FCSTD DOCUMENT  (FreeCAD 0.17R12435 (Git))
Label: JST_ZE_top_entry_pad_size
License: All rights reserved
LicenseURL: http://en.wikipedia.org/wiki/All_rights_reserved
objects: Sketcher::SketchObject×1, PartDesign::Body×1, Spreadsheet::Sheet×1
note: 2 computed .brp shape members not serialized (recipe doc carries the construction recipe); baked Part::Feature solids carry a one-line shape summary decoded from their .brp

FEATURE [Sketcher::SketchObject] Sketch
  MapMode = 5
  Support = -> [XY_Plane]
  expr: Constraints[3] = 0.75 / 2
  sketch-geometry (26):
    g0: Circle CenterX=0 CenterY=0 CenterZ=0 NormalX=0 NormalY=0 NormalZ=1 AngleXU=0 Radius=0.375
    g1: Circle CenterX=1.5 CenterY=2 CenterZ=0 NormalX=0 NormalY=0 NormalZ=1 AngleXU=0 Radius=0.375
    g2: ArcOfCircle CenterX=1.5 CenterY=2.175 CenterZ=0 NormalX=0 NormalY=0 NormalZ=1 AngleXU=0 Radius=0.7 StartAngle=0 EndAngle=3.14159
    g3: ArcOfCircle CenterX=1.5 CenterY=1.825 CenterZ=0 NormalX=0 NormalY=0 NormalZ=1 AngleXU=0 Radius=0.7 StartAngle=3.14159 EndAngle=6.28319
    g4: LineSegment StartX=0.8 StartY=2.175 StartZ=0 EndX=0.8 EndY=1.825 EndZ=0
    g5: LineSegment StartX=2.2 StartY=2.175 StartZ=0 EndX=2.2 EndY=1.825 EndZ=0
    g6: ArcOfCircle CenterX=0 CenterY=0.175 CenterZ=0 NormalX=0 NormalY=0 NormalZ=1 AngleXU=0 Radius=0.7 StartAngle=0 EndAngle=3.14159
    g7: ArcOfCircle CenterX=0 CenterY=-0.175 CenterZ=0 NormalX=0 NormalY=0 NormalZ=1 AngleXU=0 Radius=0.7 StartAngle=3.14159 EndAngle=6.28319
    g8: LineSegment StartX=-0.7 StartY=0.175 StartZ=0 EndX=-0.7 EndY=-0.175 EndZ=0
    g9: LineSegment StartX=0.7 StartY=0.175 StartZ=0 EndX=0.7 EndY=-0.175 EndZ=0
    g10: LineSegment [constr] StartX=1.5 StartY=2.175 StartZ=0 EndX=1.5 EndY=2 EndZ=0
    g11: LineSegment [constr] StartX=1.5 StartY=1.825 StartZ=0 EndX=1.5 EndY=2 EndZ=0
    g12: LineSegment [constr] StartX=0 StartY=0.175 StartZ=0 EndX=0 EndY=0 EndZ=0
    g13: LineSegment [constr] StartX=0 StartY=0 StartZ=0 EndX=0 EndY=-0.175 EndZ=0
    g14: GeomPoint X=0 Y=-0.875 Z=0
    g15: GeomPoint X=0 Y=0.875 Z=0
    g16: LineSegment [constr] StartX=0 StartY=1.16495 StartZ=0 EndX=1.16495 EndY=0 EndZ=0
    g17: LineSegment [constr] StartX=0 StartY=2.33505 StartZ=0 EndX=2.33505 EndY=0 EndZ=0
    g18: LineSegment [constr] StartX=1.75 StartY=0.585051 StartZ=0 EndX=1.16495 EndY=0 EndZ=0
    g19: GeomPoint X=0 Y=0.375 Z=0
    g20: LineSegment [constr] StartX=-0.7 StartY=0.875 StartZ=0 EndX=0.7 EndY=0.875 EndZ=0
    g21: LineSegment [constr] StartX=0.7 StartY=0.875 StartZ=0 EndX=0.7 EndY=-0.875 EndZ=0
    g22: LineSegment [constr] StartX=0.7 StartY=-0.875 StartZ=0 EndX=-0.7 EndY=-0.875 EndZ=0
    g23: LineSegment [constr] StartX=-0.7 StartY=-0.875 StartZ=0 EndX=-0.7 EndY=0.875 EndZ=0
    g24: LineSegment [constr] StartX=0 StartY=1.575 StartZ=0 EndX=1.575 EndY=0 EndZ=0
    g25: LineSegment [constr] StartX=1.575 StartY=0 StartZ=0 EndX=1.95503 EndY=0.380025 EndZ=0
  constraints (73):
    c: Coincident(g0,g-1)
    c: DistanceX(g-1,g1) = 1.5
    c: DistanceY(g-1,g1) = 2
    c: Radius(g1) = 0.375
    c: Equal(g1,g0)
    c: Tangent(g2,g5) = 1.5708
    c: Tangent(g2,g4) = -1.5708
    c: Tangent(g4,g3) = -1.5708
    c: Tangent(g5,g3) = 1.5708
    c: Vertical(g4)
    c: Equal(g2,g3)
    c: Tangent(g6,g9) = 1.5708
    c: Tangent(g6,g8) = -1.5708
    c: Tangent(g8,g7) = -1.5708
    c: Tangent(g9,g7) = 1.5708
    c: Vertical(g8)
    c: Equal(g6,g7)
    c: Coincident(g10,g2)
    c: Vertical(g10)
    c: Coincident(g11,g3)
    c: Coincident(g11,g10)
    c: Coincident(g12,g6)
    c: Vertical(g12)
    c: Coincident(g12,g13)
    c: Coincident(g13,g7)
    c: Equal(g12,g13)
    c: Equal(g13,g10)
    c: Equal(g10,g11)
    c: Equal(g6,g2)
    c: Coincident(g10,g1)
    c: Coincident(g12,g-1)
    c: DistanceX(g6,g3) = 0.1
    c: PointOnObject(g14,g-2)
    c: PointOnObject(g15,g-2)
    c: PointOnObject(g15,g6)
    c: PointOnObject(g14,g7)
    c: DistanceY(g14,g15) = 1.75
    c: PointOnObject(g18,g17)
    c: Perpendicular(g17,g18)
    c: Perpendicular(g16,g18)
    c: Angle(g16,g-1) = 0.785398
    c: Distance(g18) = 0.827386
    c: PointOnObject(g16,g-1)
    c: PointOnObject(g17,g-1)
    c: PointOnObject(g17,g-2)
    c: PointOnObject(g16,g-2)
    c: Coincident(g18,g16)
    c: Tangent(g16,g6)
    c: Tangent(g17,g3)
    c: DistanceX(g7,g7) = 1.4
    c: PointOnObject(g19,g-2)
    c: PointOnObject(g19,g0)
    c: DistanceY(g19,g15) = 0.5
    c: Coincident(g20,g21)
    c: Coincident(g21,g22)
    c: Coincident(g22,g23)
    c: Coincident(g23,g20)
    c: Horizontal(g20)
    c: Horizontal(g22)
    c: Vertical(g21)
    c: Vertical(g23)
    c: PointOnObject(g6,g23)
    c: PointOnObject(g6,g21)
    c: PointOnObject(g15,g20)
    c: PointOnObject(g14,g22)
    c: PointOnObject(g24,g-2)
    c: PointOnObject(g24,g-1)
    c: Parallel(g24,g17)
    c: PointOnObject(g20,g24)
    c: Coincident(g25,g24)
    c: PointOnObject(g25,g17)
    c: Perpendicular(g17,g25)
    c: Distance(g25) = 0.537437
FEATURE [PartDesign::Body] Body
  Group = -> [Sketch]
  Origin = -> Origin
FEATURE [Spreadsheet::Sheet] Spreadsheet
  cells = A1=Pad to Pad clearance; B1(Pad_to_Pad_clearance)=0.80000000000000004
